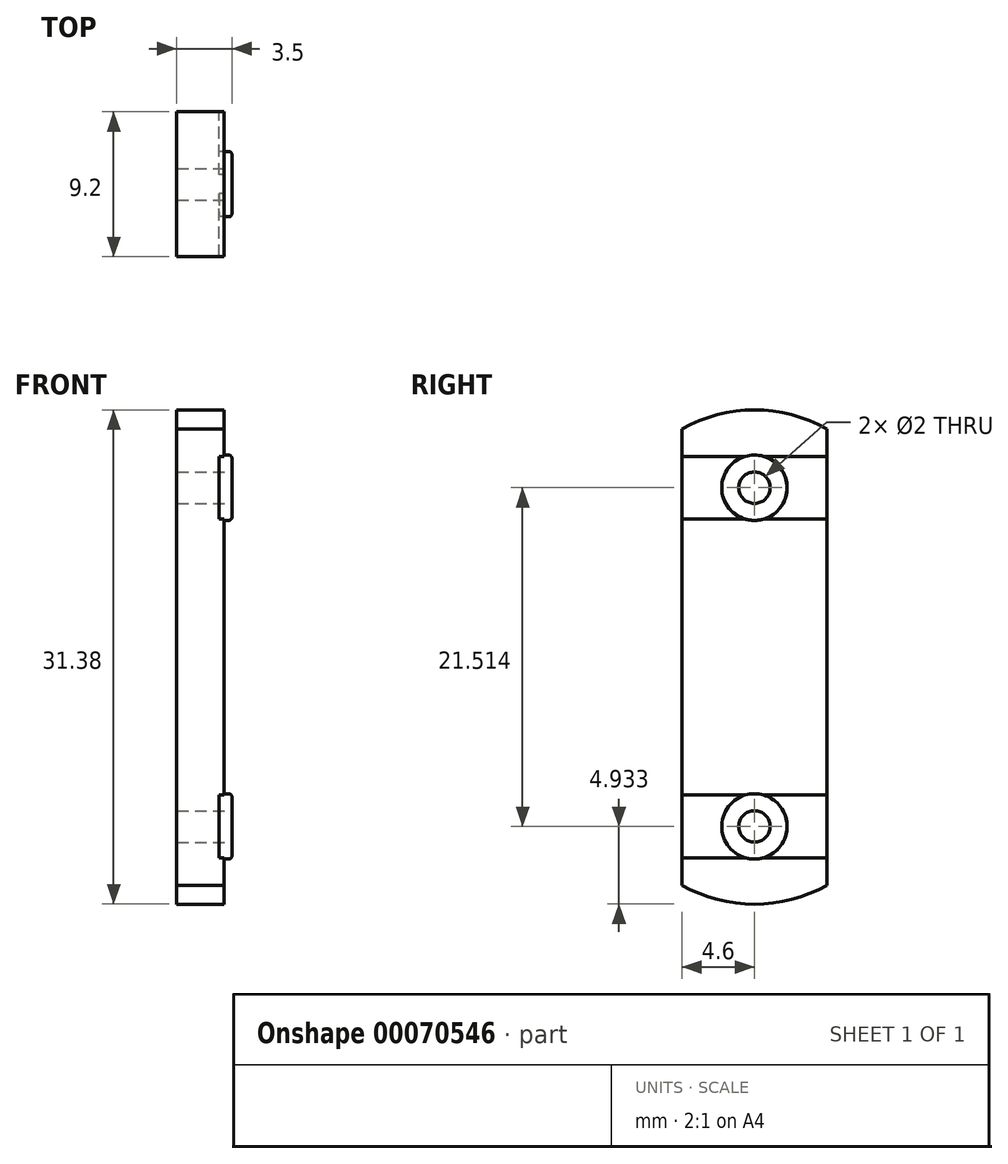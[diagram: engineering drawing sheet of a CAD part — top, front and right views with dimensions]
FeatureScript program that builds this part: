
annotation { "Feature Type Name" : "Feature", "Feature Type Description" : "" }
export const myFeature = defineFeature(function(context is Context, id is Id, definition is map)
    precondition{}
    {
        {
            var Q0;
            Q0=qCreatedBy(makeId("Right.planeOp"),FACE);
            var sketch = newSketch(context, id + "F0", { "sketchPlane" : qUnion([Q0])});
            skLineSegment(sketch, "E0", {"start": v(0, 35.43) * mm, "end": v(0, -37.29) * mm, "construction": true});
            skLineSegment(sketch, "E1", {"start": v(-31.83, 0) * mm, "end": v(31.6, 0) * mm, "construction": true});
            skLineSegment(sketch, "E2.left", {"start": v(4.6, 14.5) * mm, "end": v(4.6, -14.5) * mm});
            skLineSegment(sketch, "E2.right", {"start": v(-4.6, 14.5) * mm, "end": v(-4.6, -14.5) * mm});
            skPoint(sketch, "E2.middle", {"position": v(0, 0) * mm});
            skArc(sketch, "E3", {"start": v(-4.6, -14.5) * mm, "mid": v(0, -15.7) * mm, "end": v(4.6, -14.5) * mm});
            skArc(sketch, "E4.MirrorCS", {"start": v(-4.6, 14.5) * mm, "mid": v(0, 15.7) * mm, "end": v(4.6, 14.5) * mm});
            skSolve(sketch);
        }
        {
            var Q0;
            Q0=makeQuery(id+"F0.imprint","IMPRINT",FACE,{"disambiguationData":[TD([[makeQuery(id+"F0.imprint","IMPRINT",EDGE,{"derivedFrom":sQuery(id+"F0.wireOp",EDGE,"E2.left")}),-1.0]])]});
            extrude(context, id + "F1", {"entities" : qUnion([Q0]), "depth" : 3 * mm});
        }
        {
            var Q0;
            Q0=makeQuery(id+"F1.opExtrude","CAP_FACE",FACE,{"disambiguationData":[OSD([sQuery(id+"F0.wireOp",EDGE,"E2.left"),sQuery(id+"F0.wireOp",EDGE,"E2.right"),sQuery(id+"F0.wireOp",EDGE,"E3"),sQuery(id+"F0.wireOp",EDGE,"E4.MirrorCS")])],"isStart":false});
            var sketch = newSketch(context, id + "F2", { "sketchPlane" : qUnion([Q0])});
            skLineSegment(sketch, "E5", {"start": v(0, 19.35) * mm, "end": v(0, -7.46) * mm, "construction": true});
            skLineSegment(sketch, "E6", {"start": v(7.44, 0) * mm, "end": v(-7.44, 0) * mm, "construction": true});
            skLineSegment(sketch, "E7.bottom", {"start": v(-4.6, 12.75) * mm, "end": v(4.6, 12.75) * mm});
            skLineSegment(sketch, "E7.top", {"start": v(-4.6, 8.77) * mm, "end": v(4.6, 8.77) * mm});
            skLineSegment(sketch, "E7.left", {"start": v(-4.6, 12.75) * mm, "end": v(-4.6, 8.77) * mm});
            skLineSegment(sketch, "E7.right", {"start": v(4.6, 12.75) * mm, "end": v(4.6, 8.77) * mm});
            skLineSegment(sketch, "E8.MirrorCS", {"start": v(-4.6, -8.77) * mm, "end": v(4.6, -8.77) * mm});
            skLineSegment(sketch, "E9.MirrorCS", {"start": v(-4.6, -12.75) * mm, "end": v(-4.6, -8.77) * mm});
            skLineSegment(sketch, "E10.MirrorCS", {"start": v(-4.6, -12.75) * mm, "end": v(4.6, -12.75) * mm});
            skLineSegment(sketch, "E11.MirrorCS", {"start": v(4.6, -12.75) * mm, "end": v(4.6, -8.77) * mm});
            skSolve(sketch);
        }
        {
            var Q0;
            Q0 = qSketchRegion(id + "F2", true);
            extrude(context, id + "F3", {"entities" : qUnion([Q0]), "operationType" : NewBodyOperationType.REMOVE, "oppositeDirection" : true, "depth" : .3 * mm});
        }
        {
            var Q0;
            Q0=makeQuery(id+"F3.boolean.opBoolean","COPY",FACE,{"derivedFrom":makeQuery(id+"F3.opExtrude","CAP_FACE",FACE,{"disambiguationData":[OSD([sQuery(id+"F2.wireOp",EDGE,"E7.bottom"),sQuery(id+"F2.wireOp",EDGE,"E7.top"),sQuery(id+"F2.wireOp",EDGE,"E7.left"),sQuery(id+"F2.wireOp",EDGE,"E7.right")])],"isStart":false})});
            var sketch = newSketch(context, id + "F4", { "sketchPlane" : qUnion([Q0])});
            skLineSegment(sketch, "E12", {"start": v(0, 14.06) * mm, "end": v(0, -5.95) * mm, "construction": true});
            skLineSegment(sketch, "E13", {"start": v(7.51, 0) * mm, "end": v(-8.6, 0) * mm, "construction": true});
            skLineSegment(sketch, "E14", {"start": v(-5.3, 10.76) * mm, "end": v(6.4, 10.76) * mm, "construction": true});
            skPoint(sketch, "E14.startSnap0", {"position": v(-4.6, 10.76) * mm});
            skCircle(sketch, "E15", {"center": v(0, 10.76) * mm, "radius": 2.08 * mm});
            skCircle(sketch, "E16.MirrorC", {"center": v(0, -10.76) * mm, "radius": 2.08 * mm});
            skSolve(sketch);
        }
        {
            var Q0;
            Q0 = qSketchRegion(id + "F4", true);
            extrude(context, id + "F5", {"entities" : qUnion([Q0]), "operationType" : NewBodyOperationType.ADD, "depth" : .8 * mm});
        }
        {
            var Q0;
            Q0=makeQuery(id+"F5.opExtrude","CAP_EDGE",EDGE,{"disambiguationData":[OSD([sQuery(id+"F4.wireOp",EDGE,"E15")])],"isStart":false});
            var Q1;
            Q1=makeQuery(id+"F5.opExtrude","CAP_EDGE",EDGE,{"disambiguationData":[OSD([sQuery(id+"F4.wireOp",EDGE,"E16.MirrorC")])],"isStart":false});
            fillet(context, id + "F6", {"entities" : qUnion([Q0, Q1]), "radius" : .2 * mm, "tangentPropagation" : true, "allowEdgeOverflow" : false});
        }
        {
            var Q0;
            Q0=makeQuery(id+"F5.opExtrude","CAP_FACE",FACE,{"disambiguationData":[OSD([sQuery(id+"F4.wireOp",EDGE,"E15")])],"isStart":false});
            var sketch = newSketch(context, id + "F7", { "sketchPlane" : qUnion([Q0])});
            skLineSegment(sketch, "E17", {"start": v(0, 14.14) * mm, "end": v(0, 4.27) * mm, "construction": true});
            skLineSegment(sketch, "E18", {"start": v(0, 10.76) * mm, "end": v(5.37, 10.76) * mm, "construction": true});
            skLineSegment(sketch, "E19", {"start": v(5.37, 10.76) * mm, "end": v(-5.2, 10.76) * mm, "construction": true});
            skLineSegment(sketch, "E20", {"start": v(-5.2, 0) * mm, "end": v(5.69, 0) * mm, "construction": true});
            skCircle(sketch, "E21", {"center": v(0, 10.76) * mm, "radius": 1 * mm});
            skCircle(sketch, "E22.MirrorC", {"center": v(0, -10.76) * mm, "radius": 1 * mm});
            skSolve(sketch);
        }
        {
            var Q0;
            Q0 = qSketchRegion(id + "F7", true);
            extrude(context, id + "F8", {"entities" : qUnion([Q0]), "operationType" : NewBodyOperationType.REMOVE, "oppositeDirection" : true, "depth" : 25 * mm});
        }
    });
